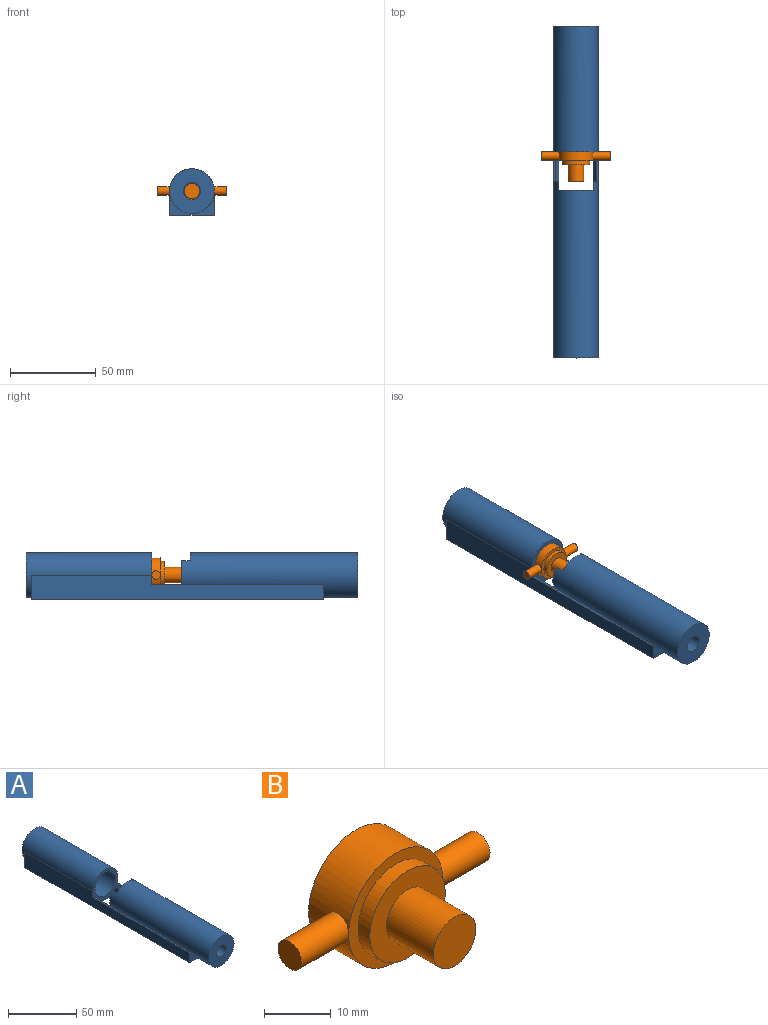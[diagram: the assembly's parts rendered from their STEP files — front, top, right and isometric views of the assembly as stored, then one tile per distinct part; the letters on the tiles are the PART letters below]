
ASSEMBLY  parts=2 mates=1
PART A: 22 faces, bbox 26x193x27 mm
  f0: cylinder r=13mm len=17.5mm, axis (0,1,0), area 58.3mm2, adj f3,f10,f14,f20
  f1: plane 170x26mm, normal (0,0,-1), area 3970mm2, adj f5,f6,f7,f10,f13,f19,f20,f21
  f2: cylinder r=13mm len=102.5mm, axis (0,1,0), area 5825.9mm2, adj f3,f7,f14,f15,f17,f18,f19,f20
  f3: plane 16.61x3mm, normal (0,1,0), area 34.1mm2, adj f0,f2,f20
  f4: cylinder r=13mm len=17.5mm, axis (0,1,0), area 58.3mm2, adj f10,f15,f18,f21
  f5: plane 170x14mm, normal (-1,0,0), area 1830mm2, adj f1,f7,f8,f10,f13,f14
  f6: plane 170x14mm, normal (1,0,0), area 1830mm2, adj f1,f7,f8,f10,f13,f15
  f7: plane 26x8.5mm, normal (0,-1,0), area 94.1mm2, adj f1,f2,f5,f6,f14,f15
  f8: cylinder r=13mm len=73mm, axis (0,1,0), area 3103.9mm2, adj f5,f6,f10,f12,f13
  f9: cylinder r=10.5mm len=70mm, axis (0,1,0), area 4618.1mm2, adj f10,f11
  f10: plane 27x26mm, normal (0,-1,0), area 237.6mm2, adj f0,f1,f4,f5,f6,f8,f9,f14
  f11: plane 21x21mm, normal (0,-1,0), area 346.4mm2, adj f9
  f12: plane 26x26mm, normal (0,1,0), area 530.9mm2, adj f8
  f13: plane 26x14mm, normal (0,1,0), area 98.5mm2, adj f1,f5,f6,f8
  f14: plane 100x1.22mm, normal (0,0,1), area 122.1mm2, adj f0,f2,f5,f7,f10
  f15: plane 100x1.22mm, normal (0,0,1), area 122.1mm2, adj f2,f4,f6,f7,f10
  f16: cylinder r=5mm len=97.5mm, axis (0,1,0), area 3063.1mm2, adj f17,f19
  f17: plane 26x26mm, normal (0,-1,0), area 452.4mm2, adj f2,f16
  f18: plane 16.61x3mm, normal (0,1,0), area 34.1mm2, adj f2,f4,f21
  f19: plane 27x20mm, normal (0,1,0), area 432.8mm2, adj f1,f2,f16,f20,f21
  f20: plane 22.5x22.31mm, normal (1,0,0), area 211.2mm2, adj f0,f1,f2,f3,f10,f19
  f21: plane 22.5x22.31mm, normal (-1,0,0), area 211.2mm2, adj f1,f2,f4,f10,f18,f19
PART B: 13 faces, bbox 40x21x20 mm
  f0: cylinder r=2.5mm len=10.32mm, axis (1,0,0), area 159.6mm2, adj f1,f2
  f1: cylinder r=10mm len=5mm, axis (0,-1,0), area 19.8mm2, adj f0
  f2: plane 5x5mm, normal (-1,0,0), area 19.6mm2, adj f0
  f3: plane 20x20mm, normal (0,-1,0), area 113.1mm2, adj f4,f5
  f4: cylinder r=8mm len=16mm, axis (0,1,0), area 125.7mm2, adj f3,f6
  f5: cylinder r=10mm len=20mm, axis (0,-1,0), area 534.1mm2, adj f3,f7
  f6: plane 16x16mm, normal (0,-1,0), area 137.4mm2, adj f4,f8
  f7: plane 20x20mm, normal (0,1,0), area 314.2mm2, adj f5
  f8: cylinder r=4.5mm len=10mm, axis (0,1,0), area 282.7mm2, adj f6,f9
  f9: plane 9x9mm, normal (0,-1,0), area 63.6mm2, adj f8
  f10: cylinder r=10mm len=5mm, axis (0,-1,0), area 19.8mm2, adj f11
  f11: cylinder r=2.5mm len=10.32mm, axis (1,0,0), area 159.6mm2, adj f10,f12
  f12: plane 5x5mm, normal (1,0,0), area 19.6mm2, adj f11
PLACE A t=(0.61,83.5,0.43)mm fixed
PLACE B t=(0.61,10.9,0.43)mm
MATE slider A.f9 <-> B.f8  axis (0,-1,0) through (0.61,83.5,0.43)mm
